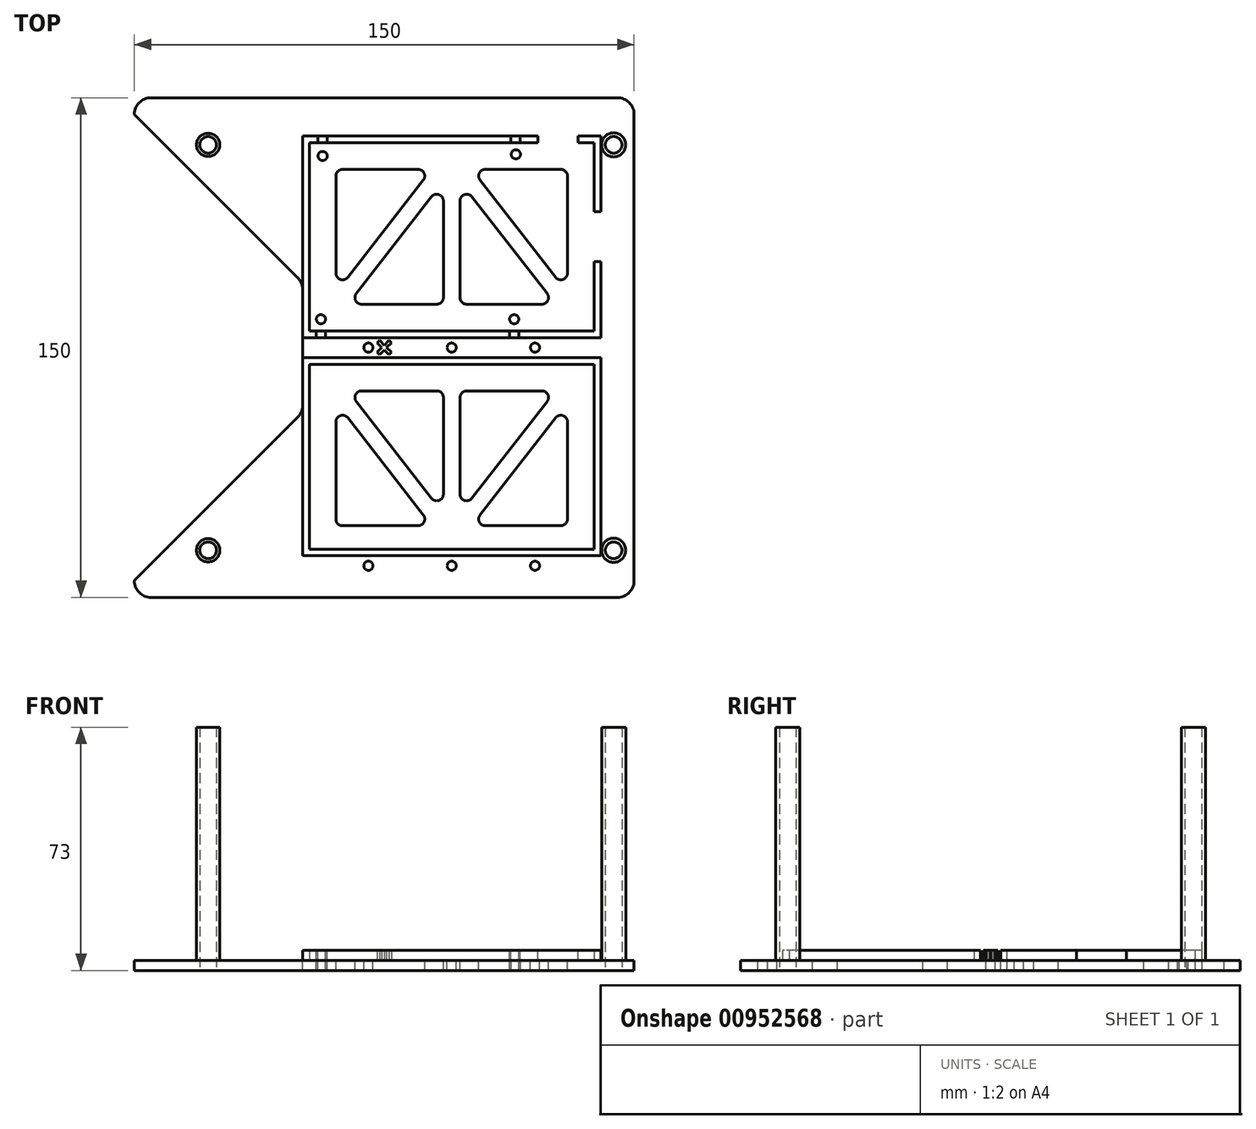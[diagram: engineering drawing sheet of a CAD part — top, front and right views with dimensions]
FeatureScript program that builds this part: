
annotation { "Feature Type Name" : "Feature", "Feature Type Description" : "" }
export const myFeature = defineFeature(function(context is Context, id is Id, definition is map)
    precondition{}
    {
        {
            var Q0;
            Q0=qCreatedBy(makeId("Top.planeOp"),FACE);
            var sketch = newSketch(context, id + "F0", { "sketchPlane" : qUnion([Q0])});
            skLineSegment(sketch, "E0.bottom", {"start": v(-75, 75) * mm, "end": v(75, 75) * mm});
            skLineSegment(sketch, "E0.top", {"start": v(-75, -75) * mm, "end": v(75, -75) * mm});
            skLineSegment(sketch, "E0.left", {"start": v(-75, 75) * mm, "end": v(-75, -75) * mm});
            skLineSegment(sketch, "E0.right", {"start": v(75, 75) * mm, "end": v(75, -75) * mm});
            skPoint(sketch, "E1", {"position": v(0, 75) * mm});
            skPoint(sketch, "E2", {"position": v(-75, 0) * mm});
            skSolve(sketch);
        }
        {
            var Q0;
            Q0 = qSketchRegion(id + "F0", true);
            extrude(context, id + "F1", {"entities" : qUnion([Q0]), "depth" : 3 * mm, "offsetDistance" : 25 * mm});
        }
        {
            var Q0;
            Q0=makeQuery(id+"F1.opExtrude","CAP_FACE",FACE,{"disambiguationData":[OSD([sQuery(id+"F0.wireOp",EDGE,"E0.bottom"),sQuery(id+"F0.wireOp",EDGE,"E0.top"),sQuery(id+"F0.wireOp",EDGE,"E0.left"),sQuery(id+"F0.wireOp",EDGE,"E0.right")])],"isStart":false});
            var sketch = newSketch(context, id + "F2", { "sketchPlane" : qUnion([Q0])});
            skLineSegment(sketch, "E3.bottom", {"start": v(-22.5, 61.5) * mm, "end": v(63, 61.5) * mm});
            skLineSegment(sketch, "E3.top", {"start": v(-22.5, 5) * mm, "end": v(63, 5) * mm});
            skLineSegment(sketch, "E3.left", {"start": v(-22.5, 61.5) * mm, "end": v(-22.5, 5) * mm});
            skLineSegment(sketch, "E3.right", {"start": v(63, 61.5) * mm, "end": v(63, 5) * mm});
            skPoint(sketch, "E4", {"position": v(20.25, 61.5) * mm});
            skLineSegment(sketch, "E5.0", {"start": v(-24.5, 63.5) * mm, "end": v(65, 63.5) * mm});
            skLineSegment(sketch, "E5.1", {"start": v(-24.5, 63.5) * mm, "end": v(-24.5, 3) * mm});
            skLineSegment(sketch, "E5.2", {"start": v(-24.5, 3) * mm, "end": v(65, 3) * mm});
            skLineSegment(sketch, "E5.3", {"start": v(65, 63.5) * mm, "end": v(65, 3) * mm});
            skSolve(sketch);
        }
        {
            var Q0;
            Q0 = qSketchRegion(id + "F2", true);
            extrude(context, id + "F3", {"entities" : qUnion([Q0]), "operationType" : NewBodyOperationType.ADD, "depth" : 3 * mm, "offsetDistance" : 25 * mm});
        }
        {
            var Q0;
            Q0=makeQuery(id+"F3.opExtrude","CAP_FACE",FACE,{"disambiguationData":[OSD([sQuery(id+"F2.wireOp",EDGE,"E3.bottom"),sQuery(id+"F2.wireOp",EDGE,"E3.top"),sQuery(id+"F2.wireOp",EDGE,"E3.left"),sQuery(id+"F2.wireOp",EDGE,"E3.right"),sQuery(id+"F2.wireOp",EDGE,"E5.0"),sQuery(id+"F2.wireOp",EDGE,"E5.1"),sQuery(id+"F2.wireOp",EDGE,"E5.2"),sQuery(id+"F2.wireOp",EDGE,"E5.3")])],"isStart":false});
            var sketch = newSketch(context, id + "F4", { "sketchPlane" : qUnion([Q0])});
            skLineSegment(sketch, "E6.bottom", {"start": v(58.15, 63.5) * mm, "end": v(46.15, 63.5) * mm});
            skLineSegment(sketch, "E6.top", {"start": v(58.15, 61.5) * mm, "end": v(46.15, 61.5) * mm});
            skLineSegment(sketch, "E6.left", {"start": v(58.15, 63.5) * mm, "end": v(58.15, 61.5) * mm});
            skLineSegment(sketch, "E6.right", {"start": v(46.15, 63.5) * mm, "end": v(46.15, 61.5) * mm});
            skPoint(sketch, "E7", {"position": v(52.15, 63.5) * mm});
            skLineSegment(sketch, "E8.bottom", {"start": v(63, 40.75) * mm, "end": v(65, 40.75) * mm});
            skLineSegment(sketch, "E8.top", {"start": v(63, 25.75) * mm, "end": v(65, 25.75) * mm});
            skLineSegment(sketch, "E8.left", {"start": v(63, 40.75) * mm, "end": v(63, 25.75) * mm});
            skLineSegment(sketch, "E8.right", {"start": v(65, 40.75) * mm, "end": v(65, 25.75) * mm});
            skPoint(sketch, "E9", {"position": v(65, 33.25) * mm});
            skSolve(sketch);
        }
        {
            var Q0;
            Q0 = qSketchRegion(id + "F4", true);
            extrude(context, id + "F5", {"entities" : qUnion([Q0]), "operationType" : NewBodyOperationType.REMOVE, "oppositeDirection" : true, "depth" : 3 * mm, "offsetDistance" : 25 * mm});
        }
        {
            var Q0;
            Q0=makeQuery(id+"F1.opExtrude","SWEPT_EDGE",EDGE,{"disambiguationData":[OSD([sQuery(id+"F0.wireOp",EDGE,"E0.bottom"),sQuery(id+"F0.wireOp",EDGE,"E0.left")])]});
            var Q1;
            Q1=makeQuery(id+"F1.opExtrude","SWEPT_EDGE",EDGE,{"disambiguationData":[OSD([sQuery(id+"F0.wireOp",EDGE,"E0.bottom"),sQuery(id+"F0.wireOp",EDGE,"E0.right")])]});
            var Q2;
            Q2=makeQuery(id+"F1.opExtrude","SWEPT_EDGE",EDGE,{"disambiguationData":[OSD([sQuery(id+"F0.wireOp",EDGE,"E0.top"),sQuery(id+"F0.wireOp",EDGE,"E0.right")])]});
            var Q3;
            Q3=makeQuery(id+"F1.opExtrude","SWEPT_EDGE",EDGE,{"disambiguationData":[OSD([sQuery(id+"F0.wireOp",EDGE,"E0.top"),sQuery(id+"F0.wireOp",EDGE,"E0.left")])]});
            fillet(context, id + "F6", {"entities" : qUnion([Q0, Q1, Q2, Q3]), "radius" : 5 * mm, "tangentPropagation" : true, "allowEdgeOverflow" : false});
        }
        {
            var Q0;
            {var subQ0=sQuery(id+"F0.wireOp",EDGE,"E0.right");var subQ1=sQuery(id+"F0.wireOp",EDGE,"E0.left");var subQ2=sQuery(id+"F0.wireOp",EDGE,"E0.top");var subQ3=sQuery(id+"F0.wireOp",EDGE,"E0.bottom");var subQ4=makeQuery(id+"F1.opExtrude","CAP_FACE",FACE,{"disambiguationData":[OSD([subQ3,subQ2,subQ1,subQ0])],"isStart":false});Q0=makeQuery(id+"F5.boolean.opBoolean","MERGE",FACE,{"derivedFrom":[makeQuery(id+"F3.boolean.opBoolean","SPLIT",FACE,{"disambiguationData":[TD([makeQuery(id+"F1.opExtrude","SWEPT_FACE",FACE,{"disambiguationData":[OSD([subQ3])]})])],"derivedFrom":subQ4}),makeQuery(id+"F3.boolean.opBoolean","SPLIT",FACE,{"disambiguationData":[TD([makeQuery(id+"F3.opExtrude","SWEPT_FACE",FACE,{"disambiguationData":[OSD([sQuery(id+"F2.wireOp",EDGE,"E3.bottom")])]})])],"derivedFrom":subQ4})],"fromTools":[makeQuery(id+"F5.opExtrude","CAP_FACE",FACE,{"disambiguationData":[OSD([sQuery(id+"F4.wireOp",EDGE,"E6.bottom"),sQuery(id+"F4.wireOp",EDGE,"E6.top"),sQuery(id+"F4.wireOp",EDGE,"E6.left"),sQuery(id+"F4.wireOp",EDGE,"E6.right")])],"isStart":false}),makeQuery(id+"F5.opExtrude","CAP_FACE",FACE,{"disambiguationData":[OSD([sQuery(id+"F4.wireOp",EDGE,"E8.bottom"),sQuery(id+"F4.wireOp",EDGE,"E8.top"),sQuery(id+"F4.wireOp",EDGE,"E8.left"),sQuery(id+"F4.wireOp",EDGE,"E8.right")])],"isStart":false})]});}
            var sketch = newSketch(context, id + "F7", { "sketchPlane" : qUnion([Q0])});
            skLineSegment(sketch, "E10.bottom", {"start": v(-22.5, -5) * mm, "end": v(63, -5) * mm});
            skLineSegment(sketch, "E10.top", {"start": v(-22.5, -60.5) * mm, "end": v(63, -60.5) * mm});
            skLineSegment(sketch, "E10.left", {"start": v(-22.5, -5) * mm, "end": v(-22.5, -60.5) * mm});
            skLineSegment(sketch, "E10.right", {"start": v(63, -5) * mm, "end": v(63, -60.5) * mm});
            skPoint(sketch, "E11", {"position": v(20.25, -5) * mm});
            skLineSegment(sketch, "E12.0", {"start": v(-24.5, -3) * mm, "end": v(65, -3) * mm});
            skLineSegment(sketch, "E12.1", {"start": v(-24.5, -3) * mm, "end": v(-24.5, -62.5) * mm});
            skLineSegment(sketch, "E12.2", {"start": v(-24.5, -62.5) * mm, "end": v(65, -62.5) * mm});
            skLineSegment(sketch, "E12.3", {"start": v(65, -3) * mm, "end": v(65, -62.5) * mm});
            skSolve(sketch);
        }
        {
            var Q0;
            Q0 = qSketchRegion(id + "F7", true);
            extrude(context, id + "F8", {"entities" : qUnion([Q0]), "operationType" : NewBodyOperationType.ADD, "depth" : 3 * mm, "offsetDistance" : 25 * mm});
        }
        {
            var Q0;
            Q0=makeQuery(id+"F7.imprint","IMPRINT",FACE,{"disambiguationData":[TD([[makeQuery(id+"F7.imprint","IMPRINT",EDGE,{"derivedFrom":sQuery(id+"F7.wireOp",EDGE,"E12.0")}),1.0]])]});
            var sketch = newSketch(context, id + "F9", { "sketchPlane" : qUnion([Q0])});
            skCircle(sketch, "E13", {"center": v(-60.86, 60.86) * mm, "radius": 3.5 * mm, "construction": true});
            skLineSegment(sketch, "E14", {"start": v(-75, 75) * mm, "end": v(75, -75) * mm, "construction": true});
            skCircle(sketch, "E15", {"center": v(-60.86, 60.86) * mm, "radius": 2.5 * mm, "construction": true});
            skCircle(sketch, "E16.MirrorC", {"center": v(60.86, 60.86) * mm, "radius": 3.5 * mm, "construction": true});
            skCircle(sketch, "E17.MirrorC", {"center": v(60.86, 60.86) * mm, "radius": 2.5 * mm, "construction": true});
            skLineSegment(sketch, "E18.MirrorCS", {"start": v(75, 75) * mm, "end": v(-75, -75) * mm, "construction": true});
            skLineSegment(sketch, "E19.MirrorCS", {"start": v(-75, -75) * mm, "end": v(75, 75) * mm, "construction": true});
            skCircle(sketch, "E20.MirrorC", {"center": v(-60.86, -60.86) * mm, "radius": 2.5 * mm, "construction": true});
            skCircle(sketch, "E21.MirrorC", {"center": v(60.86, -60.86) * mm, "radius": 2.5 * mm, "construction": true});
            skCircle(sketch, "E22.MirrorC", {"center": v(-60.86, -60.86) * mm, "radius": 3.5 * mm, "construction": true});
            skLineSegment(sketch, "E23.MirrorCS", {"start": v(75, -75) * mm, "end": v(-75, 75) * mm, "construction": true});
            skCircle(sketch, "E24.MirrorC", {"center": v(60.86, -60.86) * mm, "radius": 3.5 * mm, "construction": true});
            skCircle(sketch, "E25", {"center": v(68.86, 60.86) * mm, "radius": 3.63 * mm});
            skCircle(sketch, "E26", {"center": v(68.86, 60.86) * mm, "radius": 2.5 * mm});
            skLineSegment(sketch, "E27", {"start": v(0, 0) * mm, "end": v(75, 0) * mm, "construction": true});
            skCircle(sketch, "E28.MirrorC", {"center": v(68.86, -60.86) * mm, "radius": 2.5 * mm});
            skCircle(sketch, "E29.MirrorC", {"center": v(68.86, -60.86) * mm, "radius": 3.63 * mm});
            skCircle(sketch, "E30", {"center": v(-52.86, 60.86) * mm, "radius": 2.5 * mm});
            skCircle(sketch, "E31", {"center": v(-52.86, 60.86) * mm, "radius": 3.5 * mm});
            skCircle(sketch, "E32.MirrorC", {"center": v(-52.86, -60.86) * mm, "radius": 3.5 * mm});
            skCircle(sketch, "E33.MirrorC", {"center": v(-52.86, -60.86) * mm, "radius": 2.5 * mm});
            skSolve(sketch);
        }
        {
            var Q0;
            Q0 = qSketchRegion(id + "F9", true);
            extrude(context, id + "F10", {"entities" : qUnion([Q0]), "operationType" : NewBodyOperationType.ADD, "depth" : 70 * mm, "offsetDistance" : 25 * mm});
        }
        {
            var Q0;
            Q0=makeQuery(id+"F7.imprint","IMPRINT",FACE,{"disambiguationData":[TD([[makeQuery(id+"F7.imprint","IMPRINT",EDGE,{"derivedFrom":sQuery(id+"F7.wireOp",EDGE,"E12.0")}),1.0]])]});
            var sketch = newSketch(context, id + "F11", { "sketchPlane" : qUnion([Q0])});
            skLineSegment(sketch, "E34", {"start": v(75, 75) * mm, "end": v(0, 0) * mm, "construction": true});
            skLineSegment(sketch, "E35", {"start": v(-75, 75) * mm, "end": v(0, 0) * mm, "construction": true});
            skLineSegment(sketch, "E36", {"start": v(-1.77, 1.77) * mm, "end": v(1.77, -1.77) * mm, "construction": true});
            skLineSegment(sketch, "E37", {"start": v(1.77, 1.77) * mm, "end": v(-1.77, -1.77) * mm, "construction": true});
            skPoint(sketch, "E38", {"position": v(0, 0) * mm});
            skLineSegment(sketch, "E39", {"start": v(-2.12, 1.41) * mm, "end": v(-1.41, 2.12) * mm});
            skLineSegment(sketch, "E40", {"start": v(-1.41, 2.12) * mm, "end": v(0, 0.7) * mm});
            skLineSegment(sketch, "E41", {"start": v(0, 0.7) * mm, "end": v(1.41, 2.12) * mm});
            skLineSegment(sketch, "E42", {"start": v(1.41, 2.12) * mm, "end": v(2.12, 1.41) * mm});
            skLineSegment(sketch, "E43", {"start": v(2.12, 1.41) * mm, "end": v(0.7, 0) * mm});
            skLineSegment(sketch, "E44", {"start": v(0.7, 0) * mm, "end": v(2.12, -1.41) * mm});
            skLineSegment(sketch, "E45", {"start": v(2.12, -1.41) * mm, "end": v(1.41, -2.12) * mm});
            skLineSegment(sketch, "E46", {"start": v(1.41, -2.12) * mm, "end": v(0, -0.7) * mm});
            skLineSegment(sketch, "E47", {"start": v(0, -0.7) * mm, "end": v(-1.41, -2.12) * mm});
            skLineSegment(sketch, "E48", {"start": v(-1.41, -2.12) * mm, "end": v(-2.12, -1.41) * mm});
            skLineSegment(sketch, "E49", {"start": v(-2.12, -1.41) * mm, "end": v(-0.7, 0) * mm});
            skLineSegment(sketch, "E50", {"start": v(-0.7, 0) * mm, "end": v(-2.12, 1.41) * mm});
            skSolve(sketch);
        }
        {
            var Q0;
            Q0 = qSketchRegion(id + "F11", true);
            extrude(context, id + "F12", {"entities" : qUnion([Q0]), "operationType" : NewBodyOperationType.ADD, "depth" : 3 * mm, "offsetDistance" : 25 * mm});
        }
        {
            var Q0;
            Q0=makeQuery(id+"F7.imprint","IMPRINT",FACE,{"disambiguationData":[TD([[makeQuery(id+"F7.imprint","IMPRINT",EDGE,{"derivedFrom":sQuery(id+"F7.wireOp",EDGE,"E12.0")}),1.0]])]});
            var sketch = newSketch(context, id + "F13", { "sketchPlane" : qUnion([Q0])});
            skCircle(sketch, "E51", {"center": v(-52.86, 60.86) * mm, "radius": 2.5 * mm});
            skCircle(sketch, "E52", {"center": v(662.22, 102.26) * mm, "radius": 28.62 * mm});
            skCircle(sketch, "E53", {"center": v(693.53, -597.34) * mm, "radius": 34.48 * mm});
            skCircle(sketch, "E54", {"center": v(-44.61, -626.24) * mm, "radius": 36.14 * mm});
            skCircle(sketch, "E55", {"center": v(68.86, 60.86) * mm, "radius": 2.5 * mm});
            skCircle(sketch, "E56", {"center": v(68.86, -60.86) * mm, "radius": 2.5 * mm});
            skCircle(sketch, "E57", {"center": v(-52.86, -60.86) * mm, "radius": 2.5 * mm});
            skSolve(sketch);
        }
        {
            var Q0;
            Q0 = qSketchRegion(id + "F13", true);
            extrude(context, id + "F14", {"entities" : qUnion([Q0]), "operationType" : NewBodyOperationType.REMOVE, "oppositeDirection" : true, "depth" : 25 * mm, "offsetDistance" : 25 * mm});
        }
        {
            var Q0;
            Q0=makeQuery(id+"F2.imprint","IMPRINT",FACE,{"disambiguationData":[TD([[makeQuery(id+"F2.imprint","IMPRINT",EDGE,{"derivedFrom":sQuery(id+"F2.wireOp",EDGE,"E5.0")}),1.0]])]});
            var sketch = newSketch(context, id + "F15", { "sketchPlane" : qUnion([Q0])});
            skLineSegment(sketch, "E58", {"start": v(-75, 70) * mm, "end": v(-24.5, 19.5) * mm});
            skLineSegment(sketch, "E59", {"start": v(-24.5, 19.5) * mm, "end": v(-24.5, -19.5) * mm});
            skLineSegment(sketch, "E60", {"start": v(-24.5, -19.5) * mm, "end": v(-75, -70) * mm});
            skLineSegment(sketch, "E61", {"start": v(-75, -70) * mm, "end": v(-75, 70) * mm});
            skSolve(sketch);
        }
        {
            var Q0;
            Q0 = qSketchRegion(id + "F15", true);
            extrude(context, id + "F16", {"entities" : qUnion([Q0]), "operationType" : NewBodyOperationType.REMOVE, "oppositeDirection" : true, "depth" : 25 * mm, "offsetDistance" : 25 * mm});
        }
        {
            var Q0;
            Q0=makeQuery(id+"F16.boolean.opBoolean","COPY",EDGE,{"derivedFrom":makeQuery(id+"F16.opExtrude","SWEPT_EDGE",EDGE,{"disambiguationData":[OSD([sQuery(id+"F0.wireOp",EDGE,"E0.left"),sQuery(id+"F15.wireOp",EDGE,"E58"),sQuery(id+"F15.wireOp",EDGE,"E61")])]})});
            var Q1;
            Q1=makeQuery(id+"F16.boolean.opBoolean","COPY",EDGE,{"derivedFrom":makeQuery(id+"F16.opExtrude","SWEPT_EDGE",EDGE,{"disambiguationData":[OSD([sQuery(id+"F15.wireOp",EDGE,"E58"),sQuery(id+"F15.wireOp",EDGE,"E59")])]})});
            var Q2;
            Q2=makeQuery(id+"F16.boolean.opBoolean","COPY",EDGE,{"derivedFrom":makeQuery(id+"F16.opExtrude","SWEPT_EDGE",EDGE,{"disambiguationData":[OSD([sQuery(id+"F15.wireOp",EDGE,"E59"),sQuery(id+"F15.wireOp",EDGE,"E60")])]})});
            var Q3;
            Q3=makeQuery(id+"F16.boolean.opBoolean","COPY",EDGE,{"derivedFrom":makeQuery(id+"F16.opExtrude","SWEPT_EDGE",EDGE,{"disambiguationData":[OSD([sQuery(id+"F0.wireOp",EDGE,"E0.left"),sQuery(id+"F15.wireOp",EDGE,"E60"),sQuery(id+"F15.wireOp",EDGE,"E61")])]})});
            fillet(context, id + "F17", {"entities" : qUnion([Q0, Q1, Q2, Q3]), "radius" : 5 * mm, "tangentPropagation" : true, "allowEdgeOverflow" : false});
        }
        {
            var Q0;
            {var subQ3=sQuery(id+"F4.wireOp",EDGE,"E6.top");Q0=makeQuery(id+"F4.imprint","IMPRINT",FACE,{"disambiguationData":[TD([[makeQuery(id+"F4.imprint","IMPRINT",EDGE,{"derivedFrom":subQ3}),-1.0]])]});}
            var sketch = newSketch(context, id + "F18", { "sketchPlane" : qUnion([Q0])});
            skCircle(sketch, "E62", {"center": v(-18.5, 57.5) * mm, "radius": 1.38 * mm});
            skCircle(sketch, "E63", {"center": v(39.5, 58) * mm, "radius": 1.38 * mm});
            skCircle(sketch, "E64", {"center": v(-19, 8.5) * mm, "radius": 1.37 * mm});
            skCircle(sketch, "E65", {"center": v(39, 8.5) * mm, "radius": 1.38 * mm});
            skSolve(sketch);
        }
        {
            var Q0;
            Q0 = qSketchRegion(id + "F18", true);
            extrude(context, id + "F19", {"entities" : qUnion([Q0]), "operationType" : NewBodyOperationType.REMOVE, "oppositeDirection" : true, "depth" : 25 * mm, "offsetDistance" : 25 * mm});
        }
        {
            var Q0;
            {var subQ4=sQuery(id+"F4.wireOp",EDGE,"E6.right");Q0=makeQuery(id+"F4.imprint","IMPRINT",FACE,{"disambiguationData":[TD([[makeQuery(id+"F4.imprint","IMPRINT",EDGE,{"derivedFrom":subQ4}),-1.0]])]});}
            var sketch = newSketch(context, id + "F20", { "sketchPlane" : qUnion([Q0])});
            skLineSegment(sketch, "E66.bottom", {"start": v(-19.9, 63.5) * mm, "end": v(-17.15, 63.5) * mm});
            skLineSegment(sketch, "E66.top", {"start": v(-19.9, 61.5) * mm, "end": v(-17.15, 61.5) * mm});
            skLineSegment(sketch, "E66.left", {"start": v(-19.9, 63.5) * mm, "end": v(-19.9, 61.5) * mm});
            skLineSegment(sketch, "E66.right", {"start": v(-17.15, 63.5) * mm, "end": v(-17.15, 61.5) * mm});
            skPoint(sketch, "E67", {"position": v(-18.52, 63.5) * mm});
            skLineSegment(sketch, "E68.bottom", {"start": v(40.8, 63.5) * mm, "end": v(38.05, 63.5) * mm});
            skLineSegment(sketch, "E68.top", {"start": v(40.8, 61.5) * mm, "end": v(38.05, 61.5) * mm});
            skLineSegment(sketch, "E68.left", {"start": v(40.8, 63.5) * mm, "end": v(40.8, 61.5) * mm});
            skLineSegment(sketch, "E68.right", {"start": v(38.05, 63.5) * mm, "end": v(38.05, 61.5) * mm});
            skLineSegment(sketch, "E69.bottom", {"start": v(40.4, 5) * mm, "end": v(37.65, 5) * mm});
            skLineSegment(sketch, "E69.top", {"start": v(40.4, 3) * mm, "end": v(37.65, 3) * mm});
            skLineSegment(sketch, "E69.left", {"start": v(40.4, 5) * mm, "end": v(40.4, 3) * mm});
            skLineSegment(sketch, "E69.right", {"start": v(37.65, 5) * mm, "end": v(37.65, 3) * mm});
            skLineSegment(sketch, "E70.bottom", {"start": v(-20.4, 5) * mm, "end": v(-17.65, 5) * mm});
            skLineSegment(sketch, "E70.top", {"start": v(-20.4, 3) * mm, "end": v(-17.65, 3) * mm});
            skLineSegment(sketch, "E70.left", {"start": v(-20.4, 5) * mm, "end": v(-20.4, 3) * mm});
            skLineSegment(sketch, "E70.right", {"start": v(-17.65, 5) * mm, "end": v(-17.65, 3) * mm});
            skSolve(sketch);
        }
        {
            var Q0;
            Q0 = qSketchRegion(id + "F20", true);
            extrude(context, id + "F21", {"entities" : qUnion([Q0]), "operationType" : NewBodyOperationType.REMOVE, "oppositeDirection" : true, "depth" : 25 * mm, "offsetDistance" : 25 * mm});
        }
        {
            var Q0;
            Q0=qCreatedBy(makeId("Front.planeOp"),FACE);
            cPlane(context, id + "F22", {"entities" : qUnion([Q0]), "cplaneType" : CPlaneType.OFFSET, "offset" : 61 * mm, "width" : 150 * mm, "height" : 150 * mm});
        }
        {
            var Q0;
            Q0=makeQuery(id+"F2.imprint","IMPRINT",FACE,{"disambiguationData":[TD([[makeQuery(id+"F2.imprint","IMPRINT",EDGE,{"derivedFrom":sQuery(id+"F2.wireOp",EDGE,"E5.0")}),1.0]])]});
            var sketch = newSketch(context, id + "F23", { "sketchPlane" : qUnion([Q0])});
            skCircle(sketch, "E71", {"center": v(-4.75, 0) * mm, "radius": 1.38 * mm});
            skCircle(sketch, "E72", {"center": v(20.25, 0) * mm, "radius": 1.38 * mm});
            skCircle(sketch, "E73", {"center": v(45.25, 0) * mm, "radius": 1.38 * mm});
            skLineSegment(sketch, "E74", {"start": v(-22.5, -5) * mm, "end": v(63, -60.5) * mm, "construction": true});
            skPoint(sketch, "E75", {"position": v(20.25, -32.75) * mm});
            skLineSegment(sketch, "E76", {"start": v(0, -32.75) * mm, "end": v(20.25, -32.75) * mm, "construction": true});
            skCircle(sketch, "E77.MirrorC", {"center": v(45.25, -65.5) * mm, "radius": 1.38 * mm});
            skCircle(sketch, "E78.MirrorC", {"center": v(20.25, -65.5) * mm, "radius": 1.38 * mm});
            skCircle(sketch, "E79.MirrorC", {"center": v(-4.75, -65.5) * mm, "radius": 1.38 * mm});
            skSolve(sketch);
        }
        {
            var Q0;
            Q0 = qSketchRegion(id + "F23", true);
            extrude(context, id + "F24", {"entities" : qUnion([Q0]), "operationType" : NewBodyOperationType.REMOVE, "oppositeDirection" : true, "depth" : 25 * mm, "offsetDistance" : 25 * mm});
        }
        {
            var Q0;
            {var subQ3=sQuery(id+"F4.wireOp",EDGE,"E6.top");Q0=makeQuery(id+"F4.imprint","IMPRINT",FACE,{"disambiguationData":[TD([[makeQuery(id+"F4.imprint","IMPRINT",EDGE,{"derivedFrom":subQ3}),-1.0]])]});}
            var sketch = newSketch(context, id + "F25", { "sketchPlane" : qUnion([Q0])});
            skLineSegment(sketch, "E80.bottom", {"start": v(30.34, 53.5) * mm, "end": v(53, 53.5) * mm, "construction": true});
            skLineSegment(sketch, "E80.top", {"start": v(24.75, 13) * mm, "end": v(47.3, 13) * mm, "construction": true});
            skLineSegment(sketch, "E80.left", {"start": v(-14.5, 53.5) * mm, "end": v(-14.5, 13) * mm, "construction": true});
            skLineSegment(sketch, "E80.right", {"start": v(55, 51.5) * mm, "end": v(55, 22.33) * mm, "construction": true});
            skLineSegment(sketch, "E81", {"start": v(17.75, 53.5) * mm, "end": v(17.75, 13) * mm, "construction": true});
            skLineSegment(sketch, "E82", {"start": v(22.75, 44.02) * mm, "end": v(22.75, 15) * mm, "construction": true});
            skPoint(sketch, "E83", {"position": v(20.25, 53.5) * mm});
            skLineSegment(sketch, "E84", {"start": v(26.33, 45.25) * mm, "end": v(48.88, 16.23) * mm});
            skLineSegment(sketch, "E85", {"start": v(47.3, 13) * mm, "end": v(24.75, 13) * mm});
            skLineSegment(sketch, "E86", {"start": v(22.75, 44.02) * mm, "end": v(22.75, 15) * mm});
            skLineSegment(sketch, "E87", {"start": v(51.42, 21.1) * mm, "end": v(28.76, 50.27) * mm});
            skLineSegment(sketch, "E88", {"start": v(30.34, 53.5) * mm, "end": v(53, 53.5) * mm});
            skLineSegment(sketch, "E89", {"start": v(55, 22.33) * mm, "end": v(55, 51.5) * mm});
            skPoint(sketch, "E90.newPointA", {"position": v(-14.5, 53.5) * mm});
            skPoint(sketch, "E90.newPointB", {"position": v(26.25, 53.5) * mm});
            skArc(sketch, "E90.filletArc", {"start": v(30.34, 53.5) * mm, "mid": v(28.54, 52.38) * mm, "end": v(28.76, 50.27) * mm});
            skPoint(sketch, "E91.visualSharp", {"position": v(55, 53.5) * mm});
            skArc(sketch, "E91.filletArc", {"start": v(55, 51.5) * mm, "mid": v(54.41, 52.91) * mm, "end": v(53, 53.5) * mm});
            skPoint(sketch, "E92.newPointB", {"position": v(55, 16.5) * mm});
            skArc(sketch, "E92.filletArc", {"start": v(51.42, 21.1) * mm, "mid": v(53.65, 20.44) * mm, "end": v(55, 22.33) * mm});
            skPoint(sketch, "E93.newPointB", {"position": v(47, 13) * mm});
            skArc(sketch, "E93.filletArc", {"start": v(47.3, 13) * mm, "mid": v(49.1, 14.12) * mm, "end": v(48.88, 16.23) * mm});
            skPoint(sketch, "E94.newPointB", {"position": v(-22.5, 13) * mm});
            skArc(sketch, "E94.filletArc", {"start": v(22.75, 15) * mm, "mid": v(23.34, 13.59) * mm, "end": v(24.75, 13) * mm});
            skPoint(sketch, "E95.newPointA", {"position": v(22.75, 53.5) * mm});
            skArc(sketch, "E95.filletArc", {"start": v(26.33, 45.25) * mm, "mid": v(24.1, 45.91) * mm, "end": v(22.75, 44.02) * mm});
            skLineSegment(sketch, "E96", {"start": v(20.25, 53.5) * mm, "end": v(20.25, 12.98) * mm, "construction": true});
            skArc(sketch, "E97.MirrorCS", {"start": v(-14.5, 51.5) * mm, "mid": v(-13.91, 52.91) * mm, "end": v(-12.5, 53.5) * mm});
            skLineSegment(sketch, "E98.MirrorCS", {"start": v(17.75, 44.02) * mm, "end": v(17.75, 15) * mm});
            skLineSegment(sketch, "E99.MirrorCS", {"start": v(-6.8, 13) * mm, "end": v(15.75, 13) * mm});
            skLineSegment(sketch, "E100.MirrorCS", {"start": v(10.16, 53.5) * mm, "end": v(-12.5, 53.5) * mm});
            skLineSegment(sketch, "E101.MirrorCS", {"start": v(-14.5, 22.33) * mm, "end": v(-14.5, 51.5) * mm});
            skLineSegment(sketch, "E102.MirrorCS", {"start": v(15.75, 13) * mm, "end": v(-6.8, 13) * mm, "construction": true});
            skLineSegment(sketch, "E103.MirrorCS", {"start": v(14.17, 45.25) * mm, "end": v(-8.38, 16.23) * mm});
            skLineSegment(sketch, "E104.MirrorCS", {"start": v(-14.5, 51.5) * mm, "end": v(-14.5, 22.33) * mm, "construction": true});
            skArc(sketch, "E105.MirrorCS", {"start": v(-10.92, 21.1) * mm, "mid": v(-13.15, 20.44) * mm, "end": v(-14.5, 22.33) * mm});
            skPoint(sketch, "E106.MirrorP", {"position": v(-6.5, 13) * mm});
            skPoint(sketch, "E107.MirrorP", {"position": v(14.25, 53.5) * mm});
            skPoint(sketch, "E108.MirrorP", {"position": v(17.75, 53.5) * mm});
            skArc(sketch, "E109.MirrorCS", {"start": v(14.17, 45.25) * mm, "mid": v(16.4, 45.91) * mm, "end": v(17.75, 44.02) * mm});
            skPoint(sketch, "E110.MirrorP", {"position": v(-14.5, 16.5) * mm});
            skArc(sketch, "E111.MirrorCS", {"start": v(-6.8, 13) * mm, "mid": v(-8.6, 14.12) * mm, "end": v(-8.38, 16.23) * mm});
            skLineSegment(sketch, "E112.MirrorCS", {"start": v(17.75, 44.02) * mm, "end": v(17.75, 15) * mm, "construction": true});
            skLineSegment(sketch, "E113.MirrorCS", {"start": v(10.16, 53.5) * mm, "end": v(-12.5, 53.5) * mm, "construction": true});
            skArc(sketch, "E114.MirrorCS", {"start": v(10.16, 53.5) * mm, "mid": v(11.96, 52.38) * mm, "end": v(11.74, 50.27) * mm});
            skLineSegment(sketch, "E115.MirrorCS", {"start": v(-10.92, 21.1) * mm, "end": v(11.74, 50.27) * mm});
            skArc(sketch, "E116.MirrorCS", {"start": v(17.75, 15) * mm, "mid": v(17.16, 13.59) * mm, "end": v(15.75, 13) * mm});
            skLineSegment(sketch, "E117", {"start": v(0, 0) * mm, "end": v(72.66, 0) * mm, "construction": true});
            skArc(sketch, "E118.MirrorCS", {"start": v(-14.5, -51.5) * mm, "mid": v(-13.91, -52.91) * mm, "end": v(-12.5, -53.5) * mm});
            skArc(sketch, "E119.MirrorCS", {"start": v(22.75, -15) * mm, "mid": v(23.34, -13.59) * mm, "end": v(24.75, -13) * mm});
            skArc(sketch, "E120.MirrorCS", {"start": v(55, -51.5) * mm, "mid": v(54.41, -52.91) * mm, "end": v(53, -53.5) * mm});
            skArc(sketch, "E121.MirrorCS", {"start": v(17.75, -15) * mm, "mid": v(17.16, -13.59) * mm, "end": v(15.75, -13) * mm});
            skArc(sketch, "E122.MirrorCS", {"start": v(14.17, -45.25) * mm, "mid": v(16.4, -45.91) * mm, "end": v(17.75, -44.02) * mm});
            skLineSegment(sketch, "E123.MirrorCS", {"start": v(-14.5, -22.33) * mm, "end": v(-14.5, -51.5) * mm});
            skArc(sketch, "E124.MirrorCS", {"start": v(-6.8, -13) * mm, "mid": v(-8.6, -14.12) * mm, "end": v(-8.38, -16.23) * mm});
            skArc(sketch, "E125.MirrorCS", {"start": v(47.3, -13) * mm, "mid": v(49.1, -14.12) * mm, "end": v(48.88, -16.23) * mm});
            skArc(sketch, "E126.MirrorCS", {"start": v(-10.92, -21.1) * mm, "mid": v(-13.15, -20.44) * mm, "end": v(-14.5, -22.33) * mm});
            skArc(sketch, "E127.MirrorCS", {"start": v(30.34, -53.5) * mm, "mid": v(28.54, -52.38) * mm, "end": v(28.76, -50.27) * mm});
            skLineSegment(sketch, "E128.MirrorCS", {"start": v(17.75, -44.02) * mm, "end": v(17.75, -15) * mm});
            skArc(sketch, "E129.MirrorCS", {"start": v(26.33, -45.25) * mm, "mid": v(24.1, -45.91) * mm, "end": v(22.75, -44.02) * mm});
            skArc(sketch, "E130.MirrorCS", {"start": v(51.42, -21.1) * mm, "mid": v(53.65, -20.44) * mm, "end": v(55, -22.33) * mm});
            skArc(sketch, "E131.MirrorCS", {"start": v(10.16, -53.5) * mm, "mid": v(11.96, -52.38) * mm, "end": v(11.74, -50.27) * mm});
            skLineSegment(sketch, "E132.MirrorCS", {"start": v(17.75, -44.02) * mm, "end": v(17.75, -15) * mm, "construction": true});
            skPoint(sketch, "E133.MirrorP", {"position": v(20.25, -53.5) * mm});
            skLineSegment(sketch, "E134.MirrorCS", {"start": v(55, -22.33) * mm, "end": v(55, -51.5) * mm});
            skLineSegment(sketch, "E135.MirrorCS", {"start": v(10.16, -53.5) * mm, "end": v(-12.5, -53.5) * mm});
            skLineSegment(sketch, "E136.MirrorCS", {"start": v(47.3, -13) * mm, "end": v(24.75, -13) * mm});
            skPoint(sketch, "E137.MirrorP", {"position": v(-14.5, -53.5) * mm});
            skLineSegment(sketch, "E138.MirrorCS", {"start": v(-6.8, -13) * mm, "end": v(15.75, -13) * mm});
            skLineSegment(sketch, "E139.MirrorCS", {"start": v(22.75, -44.02) * mm, "end": v(22.75, -15) * mm});
            skLineSegment(sketch, "E140.MirrorCS", {"start": v(-14.5, -53.5) * mm, "end": v(-14.5, -13) * mm, "construction": true});
            skPoint(sketch, "E141.MirrorP", {"position": v(-22.5, -13) * mm});
            skLineSegment(sketch, "E142.MirrorCS", {"start": v(30.34, -53.5) * mm, "end": v(53, -53.5) * mm});
            skPoint(sketch, "E143.MirrorP", {"position": v(-6.5, -13) * mm});
            skPoint(sketch, "E144.MirrorP", {"position": v(47, -13) * mm});
            skPoint(sketch, "E145.MirrorP", {"position": v(17.75, -53.5) * mm});
            skLineSegment(sketch, "E146.MirrorCS", {"start": v(14.17, -45.25) * mm, "end": v(-8.38, -16.23) * mm});
            skPoint(sketch, "E147.MirrorP", {"position": v(14.25, -53.5) * mm});
            skLineSegment(sketch, "E148.MirrorCS", {"start": v(17.75, -53.5) * mm, "end": v(17.75, -13) * mm, "construction": true});
            skLineSegment(sketch, "E149.MirrorCS", {"start": v(-10.92, -21.1) * mm, "end": v(11.74, -50.27) * mm});
            skPoint(sketch, "E150.MirrorP", {"position": v(-14.5, -16.5) * mm});
            skLineSegment(sketch, "E151.MirrorCS", {"start": v(-14.5, -51.5) * mm, "end": v(-14.5, -22.33) * mm, "construction": true});
            skLineSegment(sketch, "E152.MirrorCS", {"start": v(15.75, -13) * mm, "end": v(-6.8, -13) * mm, "construction": true});
            skPoint(sketch, "E153.MirrorP", {"position": v(22.75, -53.5) * mm});
            skPoint(sketch, "E154.MirrorP", {"position": v(55, -16.5) * mm});
            skPoint(sketch, "E155.MirrorP", {"position": v(26.25, -53.5) * mm});
            skLineSegment(sketch, "E156.MirrorCS", {"start": v(22.75, -44.02) * mm, "end": v(22.75, -15) * mm, "construction": true});
            skLineSegment(sketch, "E157.MirrorCS", {"start": v(30.34, -53.5) * mm, "end": v(53, -53.5) * mm, "construction": true});
            skPoint(sketch, "E158.MirrorP", {"position": v(55, -53.5) * mm});
            skLineSegment(sketch, "E159.MirrorCS", {"start": v(24.75, -13) * mm, "end": v(47.3, -13) * mm, "construction": true});
            skLineSegment(sketch, "E160.MirrorCS", {"start": v(20.25, -53.5) * mm, "end": v(20.25, -12.98) * mm, "construction": true});
            skLineSegment(sketch, "E161.MirrorCS", {"start": v(26.33, -45.25) * mm, "end": v(48.88, -16.23) * mm});
            skLineSegment(sketch, "E162.MirrorCS", {"start": v(10.16, -53.5) * mm, "end": v(-12.5, -53.5) * mm, "construction": true});
            skLineSegment(sketch, "E163.MirrorCS", {"start": v(51.42, -21.1) * mm, "end": v(28.76, -50.27) * mm});
            skLineSegment(sketch, "E164.MirrorCS", {"start": v(55, -51.5) * mm, "end": v(55, -22.33) * mm, "construction": true});
            skSolve(sketch);
        }
        {
            var Q0;
            Q0 = qSketchRegion(id + "F25", true);
            extrude(context, id + "F26", {"entities" : qUnion([Q0]), "operationType" : NewBodyOperationType.REMOVE, "oppositeDirection" : true, "depth" : 25 * mm, "offsetDistance" : 25 * mm});
        }
    });
